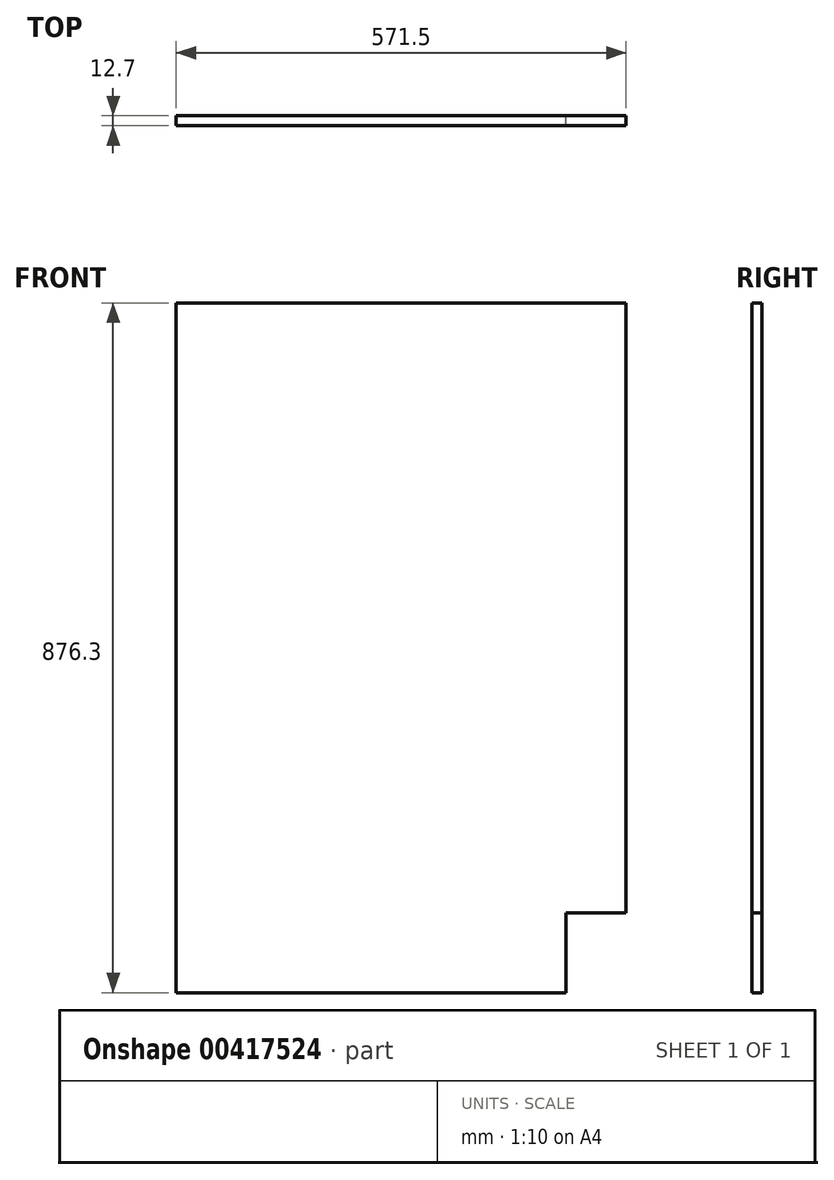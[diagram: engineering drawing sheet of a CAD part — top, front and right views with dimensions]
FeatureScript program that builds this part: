
annotation { "Feature Type Name" : "Feature", "Feature Type Description" : "" }
export const myFeature = defineFeature(function(context is Context, id is Id, definition is map)
    precondition{}
    {
        {
            var Q0;
            Q0=qCreatedBy(makeId("Front.planeOp"),FACE);
            var sketch = newSketch(context, id + "F0", { "sketchPlane" : qUnion([Q0])});
            skLineSegment(sketch, "E0.bottom", {"start": v(-285.75, 438.15) * mm, "end": v(285.75, 438.15) * mm});
            skLineSegment(sketch, "E0.top", {"start": v(-285.75, -438.15) * mm, "end": v(209.55, -438.15) * mm});
            skLineSegment(sketch, "E0.left", {"start": v(-285.75, 438.15) * mm, "end": v(-285.75, -438.15) * mm});
            skLineSegment(sketch, "E0.right", {"start": v(285.75, 438.15) * mm, "end": v(285.75, -336.55) * mm});
            skPoint(sketch, "E0.middle", {"position": v(0, 0) * mm});
            skLineSegment(sketch, "E1.0", {"start": v(209.55, -336.55) * mm, "end": v(285.75, -336.55) * mm});
            skLineSegment(sketch, "E2.0", {"start": v(209.55, -336.55) * mm, "end": v(209.55, -438.15) * mm});
            skPoint(sketch, "E3.orphan", {"position": v(285.75, -438.15) * mm});
            skSolve(sketch);
        }
        {
            var Q0;
            Q0=makeQuery(id+"F0.imprint","IMPRINT",FACE,{"disambiguationData":[TD([[makeQuery(id+"F0.imprint","IMPRINT",EDGE,{"derivedFrom":sQuery(id+"F0.wireOp",EDGE,"E0.bottom")}),-1.0]])]});
            extrude(context, id + "F1", {"entities" : qUnion([Q0]), "depth" : 12.7 * mm});
        }
    });
